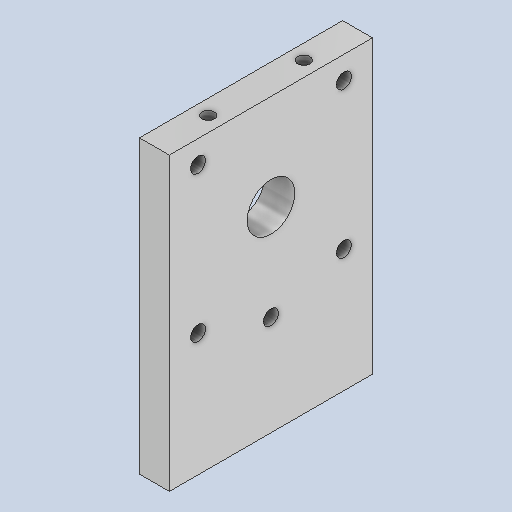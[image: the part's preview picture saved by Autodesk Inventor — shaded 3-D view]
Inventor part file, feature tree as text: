
AUTODESK INVENTOR PART (.ipt)
format: ipt  version: 2025.1 (Build 291241020, 241B)  size: 301,568 bytes
history: native  units: in
note: dims shown in document units (in); Inventor stores cm internally (conversion verified against a paired STEP export)
features: sketch x8, extrude x7, hole x1, projected_geometry x1
ambient origin geometry x8: Origin, YZ Plane, XZ Plane, XY Plane, X Axis, Y Axis, Z Axis, Center Point
bodies: Solid1 (feature_tree)
feature tree (17):
  extrude  "Extrusion1"  Depth=2.5in
  extrude  "Extrusion2"  Depth=0.0625in
  extrude  "Extrusion3"  Depth=0.0625in
  extrude  "Extrusion4"  Depth=0.3976in
  extrude  "Extrusion5"  TaperAngle=0.0deg  [1 undecoded]
  extrude  "Extrusion6"  Depth=0.8in
  extrude  "Extrusion7"  Depth=0.6in
  hole  "Hole1"  [1 undecoded]
  sketch  "Sketch1"  dims[d0=11.0in d1=2.5in]
  sketch  "Sketch2"  dims[d2=1.7in d3=0.0in d4=0.0625in]
  sketch  "Sketch3"  dims[d5=0.0625in d6=0.0625in]
  sketch  "Sketch4"  dims[d7=1.5in d8=0.0in d9=0.3976in]
  sketch  "Sketch5"  dims[d10=0.8in d11=0.0in d12=0.0in]
  sketch  "Sketch6"  dims[d13=0.125in d15=0.8in]
  sketch  "Sketch7"  dims[d16=0.4in d17=0.6in]
  projected_geometry  "Projected Loop1"
  sketch  "Sketch8"  dims[d18=0.1875in d19=1.0in d20=0.0in d21=0.125in d22=0.6102in d23=0.6102in d24=1.0in d25=0.0in d26=0.0in d27=0.0in d28=0.25in d29=0.0in d30=0.45in d31=0.45in d32=0.104in d33=0.276in d34=0.375in d35=0.25in d36=0.5635in d37=0.432in d38=0.8108in d39=0.75in d40=0.8108in d41=0.0625in d42=0.75in d43=0.375in]
note: 2 required parameter values undecoded (feature->parameter linkage not recoverable at this tier; creation-order binding heuristic only, values carry confidence <= 0.55)
